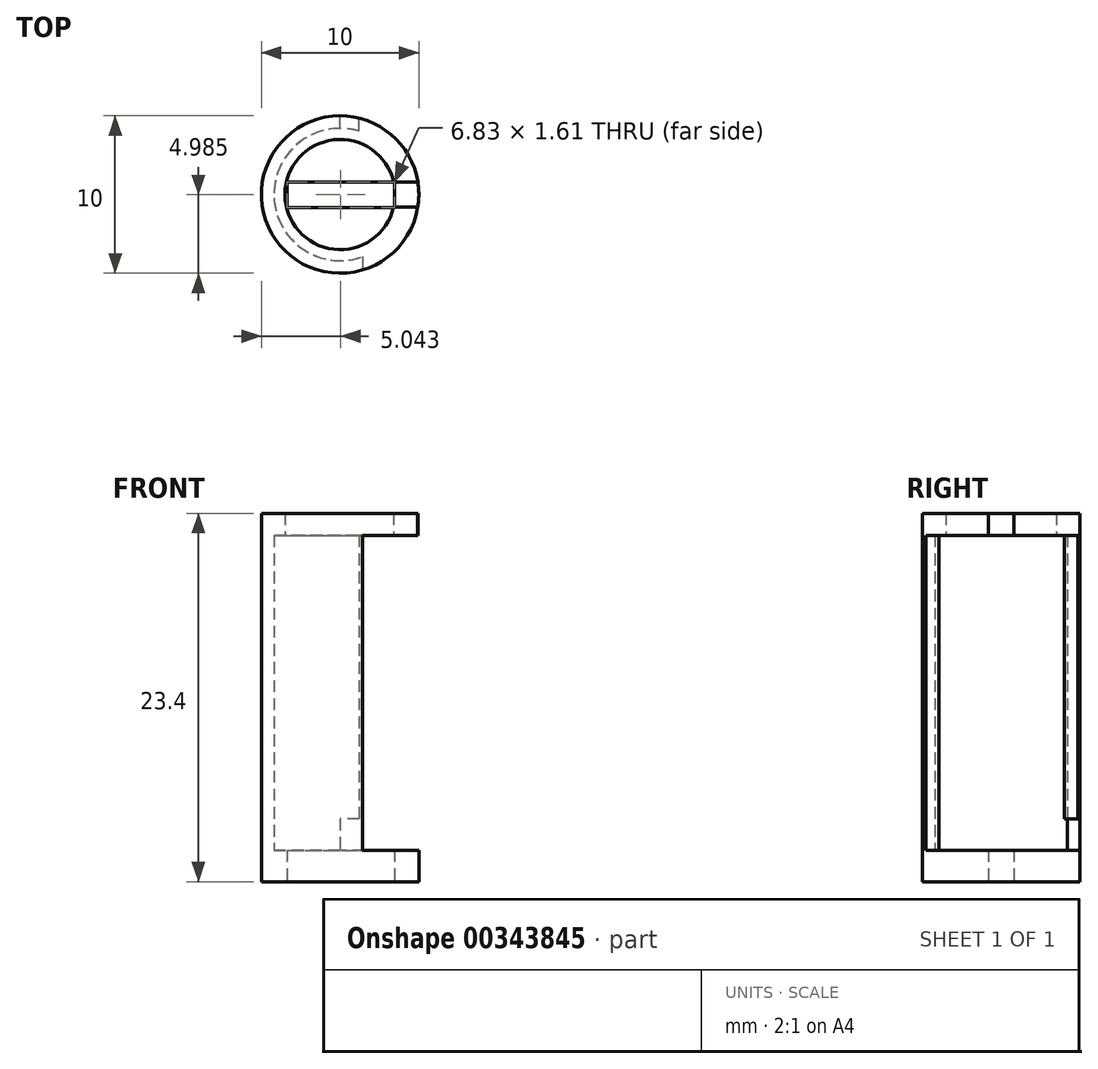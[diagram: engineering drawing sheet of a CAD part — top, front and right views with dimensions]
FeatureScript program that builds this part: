
annotation { "Feature Type Name" : "Feature", "Feature Type Description" : "" }
export const myFeature = defineFeature(function(context is Context, id is Id, definition is map)
    precondition{}
    {
        {
            var Q0;
            Q0=qCreatedBy(makeId("Top.planeOp"),FACE);
            var sketch = newSketch(context, id + "F0", { "sketchPlane" : qUnion([Q0])});
            skCircle(sketch, "E0", {"center": v(0, 0) * mm, "radius": 5 * mm});
            skLineSegment(sketch, "E1.bottom", {"start": v(-3.37, 0.8) * mm, "end": v(3.46, 0.8) * mm});
            skLineSegment(sketch, "E1.top", {"start": v(-3.37, -0.82) * mm, "end": v(3.46, -0.82) * mm});
            skLineSegment(sketch, "E1.left", {"start": v(-3.37, 0.8) * mm, "end": v(-3.37, -0.82) * mm});
            skLineSegment(sketch, "E1.right", {"start": v(3.46, 0.8) * mm, "end": v(3.46, -0.82) * mm});
            skArc(sketch, "E2", {"start": v(1.21, 4.02) * mm, "mid": v(-4.2, -0.1) * mm, "end": v(1.42, -3.95) * mm});
            skLineSegment(sketch, "E3", {"start": v(1.21, 4.02) * mm, "end": v(1.21, 4.85) * mm});
            skLineSegment(sketch, "E4", {"start": v(1.42, -3.95) * mm, "end": v(1.42, -4.8) * mm});
            skSolve(sketch);
        }
        {
            var Q0;
            Q0=makeQuery(id+"F0.imprint","IMPRINT",FACE,{"disambiguationData":[TD([[makeQuery(id+"F0.imprint","IMPRINT",EDGE,{"derivedFrom":sQuery(id+"F0.wireOp",EDGE,"E1.bottom")}),1.0]])]});
            extrude(context, id + "F1", {"entities" : qUnion([Q0]), "depth" : 2 * mm});
        }
        {
            var Q0;
            Q0=makeQuery(id+"F0.imprint","IMPRINT",FACE,{"disambiguationData":[TD([[makeQuery(id+"F0.imprint","IMPRINT",EDGE,{"derivedFrom":sQuery(id+"F0.wireOp",EDGE,"E2")}),-1.0]])]});
            extrude(context, id + "F2", {"entities" : qUnion([Q0]), "operationType" : NewBodyOperationType.ADD, "depth" : 22 * mm});
        }
        {
            var Q0;
            Q0=makeQuery(id+"F2.opExtrude","CAP_FACE",FACE,{"disambiguationData":[OSD([sQuery(id+"F0.wireOp",EDGE,"E0"),sQuery(id+"F0.wireOp",EDGE,"E2"),sQuery(id+"F0.wireOp",EDGE,"E3"),sQuery(id+"F0.wireOp",EDGE,"E4")])],"isStart":false});
            var sketch = newSketch(context, id + "F3", { "sketchPlane" : qUnion([Q0])});
            skLineSegment(sketch, "E5", {"start": v(3.4, 0.8) * mm, "end": v(4.94, 0.8) * mm});
            skLineSegment(sketch, "E6", {"start": v(3.4, -0.81) * mm, "end": v(4.93, -0.81) * mm});
            skArc(sketch, "E7", {"start": v(3.4, 0.8) * mm, "mid": v(-3.5, 0) * mm, "end": v(3.4, -0.81) * mm});
            skArc(sketch, "E8", {"start": v(4.94, 0.8) * mm, "mid": v(-5, 0) * mm, "end": v(4.93, -0.81) * mm});
            skSolve(sketch);
        }
        {
            var Q0;
            Q0 = qSketchRegion(id + "F3", true);
            extrude(context, id + "F4", {"entities" : qUnion([Q0]), "operationType" : NewBodyOperationType.ADD, "depth" : 1.4 * mm});
        }
        {
            var Q0;
            Q0=makeQuery(id+"F1.opExtrude","CAP_FACE",FACE,{"disambiguationData":[OSD([sQuery(id+"F0.wireOp",EDGE,"E0"),sQuery(id+"F0.wireOp",EDGE,"E1.bottom"),sQuery(id+"F0.wireOp",EDGE,"E1.top"),sQuery(id+"F0.wireOp",EDGE,"E1.left"),sQuery(id+"F0.wireOp",EDGE,"E1.right"),sQuery(id+"F0.wireOp",EDGE,"E2"),sQuery(id+"F0.wireOp",EDGE,"E3"),sQuery(id+"F0.wireOp",EDGE,"E4")])],"isStart":false});
            var sketch = newSketch(context, id + "F5", { "sketchPlane" : qUnion([Q0])});
            skLineSegment(sketch, "E9.bottom", {"start": v(0, 4.02) * mm, "end": v(1.21, 4.02) * mm});
            skLineSegment(sketch, "E9.top", {"start": v(0, 5.03) * mm, "end": v(1.21, 5.03) * mm});
            skLineSegment(sketch, "E9.left", {"start": v(0, 4.02) * mm, "end": v(0, 5.03) * mm});
            skLineSegment(sketch, "E9.right", {"start": v(1.21, 4.02) * mm, "end": v(1.21, 5.03) * mm});
            skSolve(sketch);
        }
        {
            var Q0;
            Q0 = qSketchRegion(id + "F5", true);
            extrude(context, id + "F6", {"entities" : qUnion([Q0]), "operationType" : NewBodyOperationType.REMOVE, "depth" : 2 * mm});
        }
    });
